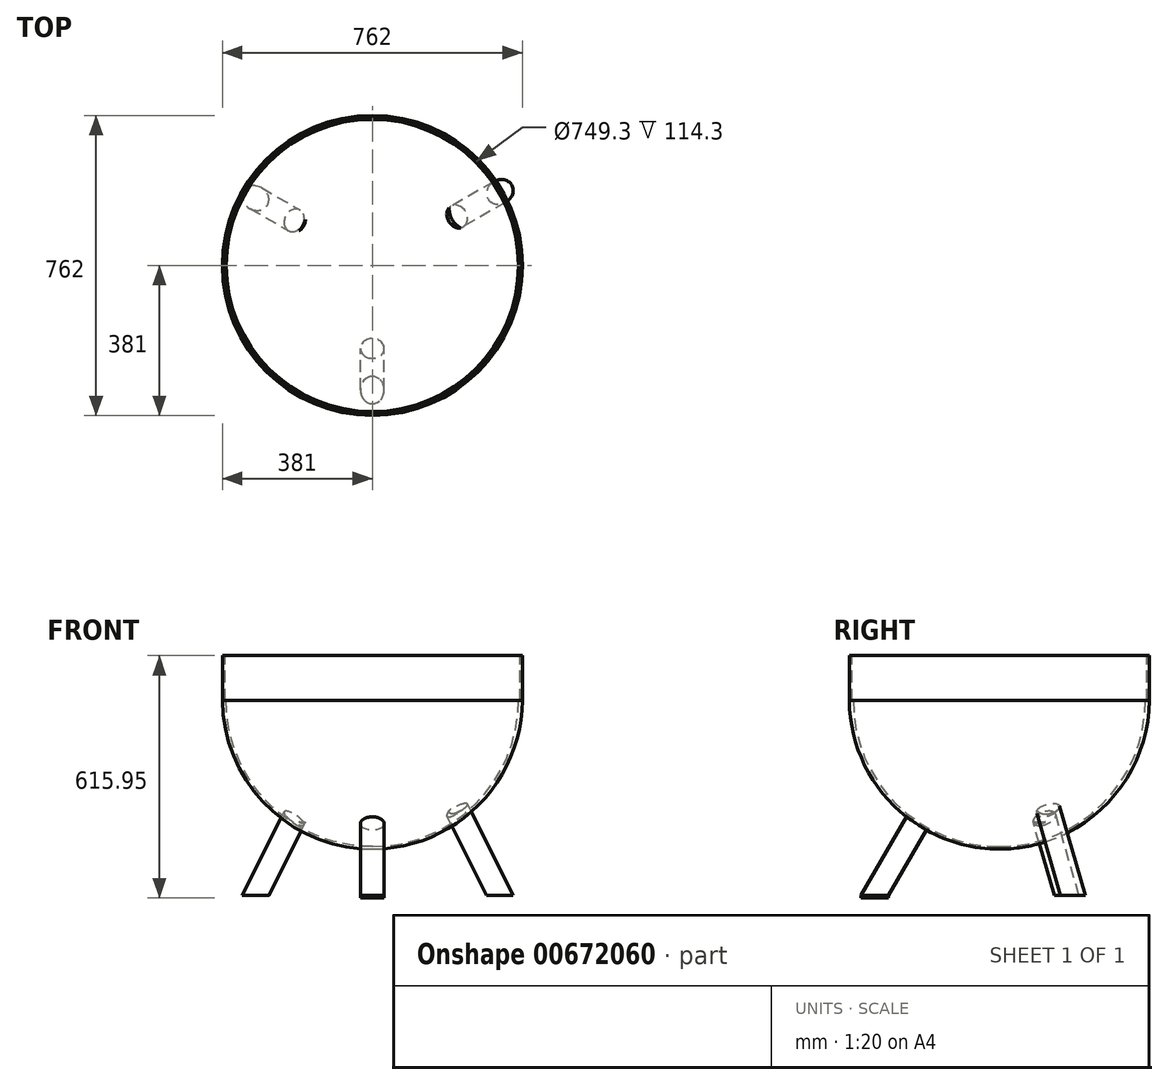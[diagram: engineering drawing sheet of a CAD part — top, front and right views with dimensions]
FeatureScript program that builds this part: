
annotation { "Feature Type Name" : "Feature", "Feature Type Description" : "" }
export const myFeature = defineFeature(function(context is Context, id is Id, definition is map)
    precondition{}
    {
        {
            var Q0;
            Q0=qCreatedBy(makeId("Top.planeOp"),FACE);
            var sketch = newSketch(context, id + "F0", { "sketchPlane" : qUnion([Q0])});
            skCircle(sketch, "E0.cCircle", {"center": v(0, 0) * mm, "radius": 527.93 * mm, "construction": true});
            skLineSegment(sketch, "E0.0", {"start": v(304.8, 527.93) * mm, "end": v(609.6, 0) * mm});
            skLineSegment(sketch, "E0.1", {"start": v(609.6, 0) * mm, "end": v(457.2, -263.96) * mm});
            skLineSegment(sketch, "E0.2", {"start": v(304.8, -527.93) * mm, "end": v(-304.8, -527.93) * mm});
            skLineSegment(sketch, "E0.3", {"start": v(-304.8, -527.93) * mm, "end": v(-457.2, -263.96) * mm});
            skLineSegment(sketch, "E0.4", {"start": v(-609.6, 0) * mm, "end": v(-450.85, 274.96) * mm});
            skLineSegment(sketch, "E0.5", {"start": v(-304.8, 527.93) * mm, "end": v(0, 527.93) * mm});
            skPoint(sketch, "E0.0.midPoint", {"position": v(457.2, 263.96) * mm});
            skCircle(sketch, "E1", {"center": v(0, 0) * mm, "radius": 381 * mm});
            skLineSegment(sketch, "E2", {"start": v(-463.55, 252.97) * mm, "end": v(-336.12, 179.4) * mm});
            skLineSegment(sketch, "E3", {"start": v(-450.85, 274.96) * mm, "end": v(-323.42, 201.4) * mm});
            skLineSegment(sketch, "E4", {"start": v(-304.8, 527.93) * mm, "end": v(-304.8, 527.93) * mm});
            skLineSegment(sketch, "E5", {"start": v(-463.55, 252.97) * mm, "end": v(-304.8, 527.93) * mm});
            skLineSegment(sketch, "E6", {"start": v(-450.85, 274.96) * mm, "end": v(-401.2, 360.95) * mm});
            skLineSegment(sketch, "E7", {"start": v(-609.6, 0) * mm, "end": v(-609.6, 0) * mm});
            skLineSegment(sketch, "E8.1.0", {"start": v(-450.85, -274.96) * mm, "end": v(-323.42, -201.4) * mm});
            skLineSegment(sketch, "E8.1.1", {"start": v(-463.55, -252.97) * mm, "end": v(-336.12, -179.4) * mm});
            skLineSegment(sketch, "E8.2.0", {"start": v(12.7, -527.93) * mm, "end": v(12.7, -380.79) * mm});
            skLineSegment(sketch, "E8.2.1", {"start": v(-12.7, -527.93) * mm, "end": v(-12.7, -380.79) * mm});
            skLineSegment(sketch, "E8.3.0", {"start": v(463.55, -252.97) * mm, "end": v(336.12, -179.4) * mm});
            skLineSegment(sketch, "E8.3.1", {"start": v(450.85, -274.96) * mm, "end": v(323.42, -201.4) * mm});
            skLineSegment(sketch, "E8.4.0", {"start": v(450.85, 274.96) * mm, "end": v(323.42, 201.4) * mm});
            skLineSegment(sketch, "E8.4.1", {"start": v(463.55, 252.97) * mm, "end": v(336.12, 179.4) * mm});
            skLineSegment(sketch, "E8.5.0", {"start": v(-12.7, 527.93) * mm, "end": v(-12.7, 380.79) * mm});
            skLineSegment(sketch, "E8.5.1", {"start": v(12.7, 527.93) * mm, "end": v(12.7, 380.79) * mm});
            skLineSegment(sketch, "E9", {"start": v(-1099.5, 381) * mm, "end": v(1284.02, 381) * mm, "construction": true});
            skLineSegment(sketch, "E10", {"start": v(-1101.82, -381) * mm, "end": v(1466.6, -381) * mm, "construction": true});
            skLineSegment(sketch, "E11", {"start": v(127, -73.32) * mm, "end": v(-127, -73.32) * mm});
            skCircle(sketch, "E12", {"center": v(0, 0) * mm, "radius": 146.65 * mm, "construction": true});
            skLineSegment(sketch, "E13", {"start": v(0, 0) * mm, "end": v(329.96, -190.5) * mm, "construction": true});
            skLineSegment(sketch, "E14", {"start": v(0, 0) * mm, "end": v(-329.96, -190.5) * mm, "construction": true});
            skLineSegment(sketch, "E15", {"start": v(0, 0) * mm, "end": v(0, 381) * mm, "construction": true});
            skLineSegment(sketch, "E16", {"start": v(329.96, -190.5) * mm, "end": v(1171.58, -676.41) * mm, "construction": true});
            skLineSegment(sketch, "E17", {"start": v(457.2, -263.96) * mm, "end": v(304.8, -527.93) * mm});
            skLineSegment(sketch, "E18", {"start": v(329.96, -190.5) * mm, "end": v(457.2, -263.96) * mm});
            skLineSegment(sketch, "E19", {"start": v(0, 381) * mm, "end": v(0, 1090.4) * mm, "construction": true});
            skLineSegment(sketch, "E20", {"start": v(0, 527.93) * mm, "end": v(304.8, 527.93) * mm});
            skLineSegment(sketch, "E21", {"start": v(0, 527.93) * mm, "end": v(0, 381) * mm});
            skLineSegment(sketch, "E22", {"start": v(-329.96, -190.5) * mm, "end": v(-1262.9, -729.14) * mm, "construction": true});
            skLineSegment(sketch, "E23", {"start": v(-457.2, -263.96) * mm, "end": v(-609.6, 0) * mm});
            skLineSegment(sketch, "E24", {"start": v(-329.96, -190.5) * mm, "end": v(-457.2, -263.96) * mm});
            skCircle(sketch, "E25", {"center": v(0, 0) * mm, "radius": 374.65 * mm});
            skSolve(sketch);
        }
        {
            var Q0;
            {var subQ0=sQuery(id+"F0.wireOp",EDGE,"E1");var subQ8=makeQuery(id+"F0.imprint","INTERSECT",VERTEX,{"derivedFrom":[subQ0,sQuery(id+"F0.wireOp",EDGE,"E8.4.0")]});Q0=makeQuery(id+"F0.imprint","IMPRINT",FACE,{"disambiguationData":[TD([[makeQuery(id+"F0.imprint","IMPRINT",EDGE,{"disambiguationData":[TD([[subQ8,1.0]])],"derivedFrom":subQ0}),1.0]])]});}
            extrude(context, id + "F1", {"entities" : qUnion([Q0]), "oppositeDirection" : true, "depth" : 152.4 * mm, "offsetDistance" : 25.4 * mm, "hasSecondDirection" : true, "secondDirectionOppositeDirection" : true, "secondDirectionDepth" : 38.1 * mm});
        }
        {
            var Q0;
            Q0=qCreatedBy(makeId("Front.planeOp"),FACE);
            var sketch = newSketch(context, id + "F2", { "sketchPlane" : qUnion([Q0])});
            skLineSegment(sketch, "E26", {"start": v(0, 608.83) * mm, "end": v(0, -1105.26) * mm, "construction": true});
            skLineSegment(sketch, "E27", {"start": v(-381, 462.6) * mm, "end": v(-381, -843.09) * mm});
            skLineSegment(sketch, "E28.MirrorCS", {"start": v(381, 462.6) * mm, "end": v(381, -843.09) * mm});
            skLineSegment(sketch, "E29", {"start": v(-1108.33, -152.4) * mm, "end": v(1492.5, -152.4) * mm, "construction": true});
            skArc(sketch, "E30", {"start": v(-381, -152.4) * mm, "mid": v(-268.19, -419.57) * mm, "end": v(0, -529.94) * mm});
            skArc(sketch, "E31", {"start": v(0, -529.94) * mm, "mid": v(268.19, -419.57) * mm, "end": v(381, -152.4) * mm});
            skLineSegment(sketch, "E32", {"start": v(-495.68, -152.4) * mm, "end": v(0, -152.4) * mm});
            skLineSegment(sketch, "E33", {"start": v(0, 45.3) * mm, "end": v(0, -541.67) * mm});
            skLineSegment(sketch, "E34", {"start": v(0, -152.4) * mm, "end": v(518.85, -152.4) * mm});
            skCircle(sketch, "E35", {"center": v(0, -152.4) * mm, "radius": 371.19 * mm});
            skSolve(sketch);
        }
        {
            var Q0;
            Q0=sQuery(id+"F0.wireOp",EDGE,"E13");
            var Q1;
            Q1=sQuery(id+"F2.wireOp",EDGE,"E26");
            cPlane(context, id + "F3", {"entities" : qUnion([Q0, Q1]), "cplaneType" : CPlaneType.LINE_ANGLE, "offset" : 25.4 * mm, "angle" : 0 * degree, "width" : 152.4 * mm, "height" : 152.4 * mm});
        }
        {
            var Q0;
            Q0=sQuery(id+"F0.wireOp",EDGE,"E15");
            var Q1;
            Q1=sQuery(id+"F2.wireOp",EDGE,"E26");
            cPlane(context, id + "F4", {"entities" : qUnion([Q0, Q1]), "cplaneType" : CPlaneType.LINE_ANGLE, "offset" : 25.4 * mm, "angle" : 0 * degree, "width" : 152.4 * mm, "height" : 152.4 * mm});
        }
        {
            var Q0;
            Q0=sQuery(id+"F0.wireOp",EDGE,"E22");
            var Q1;
            Q1=sQuery(id+"F2.wireOp",EDGE,"E26");
            cPlane(context, id + "F5", {"entities" : qUnion([Q0, Q1]), "cplaneType" : CPlaneType.LINE_ANGLE, "offset" : 25.4 * mm, "angle" : 0 * degree, "width" : 152.4 * mm, "height" : 152.4 * mm});
        }
        {
            var Q0;
            Q0=qCreatedBy(id+"F5.planeOp",FACE);
            var sketch = newSketch(context, id + "F6", { "sketchPlane" : qUnion([Q0])});
            skLineSegment(sketch, "E36", {"start": v(-1017.96, -647.7) * mm, "end": v(-373.95, -647.7) * mm});
            skLineSegment(sketch, "E37", {"start": v(-2207.22, 0) * mm, "end": v(364.68, 0) * mm, "construction": true});
            skLineSegment(sketch, "E38", {"start": v(0, 853.8) * mm, "end": v(0, -860.28) * mm, "construction": true});
            skLineSegment(sketch, "E39", {"start": v(-381, 707.57) * mm, "end": v(-381, -944.4) * mm});
            skLineSegment(sketch, "E40", {"start": v(-2225.52, -152.4) * mm, "end": v(0, -152.4) * mm, "construction": true});
            skArc(sketch, "E41", {"start": v(-381, -152.4) * mm, "mid": v(-268.19, -419.57) * mm, "end": v(0, -529.94) * mm});
            skArc(sketch, "E42", {"start": v(0, -529.94) * mm, "mid": v(268.19, -419.57) * mm, "end": v(381, -152.4) * mm});
            skLineSegment(sketch, "E43", {"start": v(0, -152.4) * mm, "end": v(375.32, -152.4) * mm, "construction": true});
            skLineSegment(sketch, "E44", {"start": v(-1487.46, 0) * mm, "end": v(0, 0) * mm, "construction": true});
            skLineSegment(sketch, "E45", {"start": v(-470.85, 0) * mm, "end": v(0, 0) * mm, "construction": true});
            skLineSegment(sketch, "E46", {"start": v(277.13, -647.7) * mm, "end": v(310.58, -647.7) * mm});
            skLineSegment(sketch, "E47", {"start": v(0, 0) * mm, "end": v(-373.95, -647.7) * mm});
            skLineSegment(sketch, "E48", {"start": v(32.55, -3.98) * mm, "end": v(-339.1, -647.7) * mm});
            skLineSegment(sketch, "E49", {"start": v(-34.84, 0) * mm, "end": v(-408.8, -647.7) * mm});
            skLineSegment(sketch, "E50", {"start": v(-381, -647.7) * mm, "end": v(1871, -647.7) * mm});
            skLineSegment(sketch, "E51.MirrorCS", {"start": v(34.84, 0) * mm, "end": v(408.8, -647.7) * mm});
            skLineSegment(sketch, "E52.MirrorCS", {"start": v(-32.55, -3.98) * mm, "end": v(339.1, -647.7) * mm});
            skLineSegment(sketch, "E53.MirrorCS", {"start": v(0, 0) * mm, "end": v(373.95, -647.7) * mm});
            skSolve(sketch);
        }
        {
            var Q0;
            {var subQ0=sQuery(id+"F6.wireOp",EDGE,"E51.MirrorCS");var subQ1=sQuery(id+"F6.wireOp",EDGE,"E42");var subQ2=makeQuery(id+"F6.imprint","INTERSECT",VERTEX,{"derivedFrom":[subQ1,subQ0]});Q0=makeQuery(id+"F6.imprint","IMPRINT",FACE,{"disambiguationData":[TD([[makeQuery(id+"F6.imprint","IMPRINT",EDGE,{"disambiguationData":[TD([[subQ2,1.0]])],"derivedFrom":subQ1}),-1.0]])]});}
            var Q1;
            Q1=sQuery(id+"F6.wireOp",EDGE,"E53.MirrorCS");
            revolve(context, id + "F7", {"entities" : qUnion([Q0]), "axis" : qUnion([Q1]), "revolveType" : RevolveType.FULL});
        }
        {
            var Q0;
            {var subQ0=sQuery(id+"F2.wireOp",EDGE,"E31");Q0=makeQuery(id+"F2.imprint","IMPRINT",FACE,{"disambiguationData":[TD([[makeQuery(id+"F2.imprint","IMPRINT",EDGE,{"derivedFrom":subQ0}),1.0]])]});}
            var Q1;
            Q1=sQuery(id+"F2.wireOp",EDGE,"E33");
            revolve(context, id + "F8", {"entities" : qUnion([Q0]), "axis" : qUnion([Q1]), "revolveType" : RevolveType.FULL});
        }
        {
            var Q0;
            {var subQ0=sQuery(id+"F2.wireOp",EDGE,"E34");var subQ3=sQuery(id+"F2.wireOp",EDGE,"E35");var subQ5=makeQuery(id+"F2.imprint","INTERSECT",VERTEX,{"derivedFrom":[subQ0,subQ3]});Q0=makeQuery(id+"F2.imprint","IMPRINT",FACE,{"disambiguationData":[TD([[makeQuery(id+"F2.imprint","IMPRINT",EDGE,{"disambiguationData":[TD([[subQ5,1.0]])],"derivedFrom":subQ3}),1.0]])]});}
            var Q1;
            Q1=sQuery(id+"F2.wireOp",EDGE,"E33");
            revolve(context, id + "F9", {"operationType" : NewBodyOperationType.REMOVE, "entities" : qUnion([Q0]), "axis" : qUnion([Q1]), "revolveType" : RevolveType.FULL, "oppositeDirection" : true});
        }
        {
            var Q0;
            {var subQ0=sQuery(id+"F0.wireOp",EDGE,"E8.1.0");Q0=makeQuery(id+"F0.imprint","IMPRINT",FACE,{"disambiguationData":[TD([[makeQuery(id+"F0.imprint","IMPRINT",EDGE,{"derivedFrom":subQ0}),-1.0]])]});}
            cPlane(context, id + "F10", {"entities" : qUnion([Q0]), "cplaneType" : CPlaneType.OFFSET, "offset" : 647.7 * mm, "oppositeDirection" : true, "width" : 152.4 * mm, "height" : 152.4 * mm});
        }
        {
            var Q0;
            Q0=qCreatedBy(id+"F10.planeOp",FACE);
            var sketch = newSketch(context, id + "F11", { "sketchPlane" : qUnion([Q0])});
            skLineSegment(sketch, "E54.bottom", {"start": v(-408.5, 256.07) * mm, "end": v(423.7, 256.07) * mm});
            skLineSegment(sketch, "E54.top", {"start": v(-408.5, -410.84) * mm, "end": v(423.7, -410.84) * mm});
            skLineSegment(sketch, "E54.left", {"start": v(-408.5, 256.07) * mm, "end": v(-408.5, -410.84) * mm});
            skLineSegment(sketch, "E54.right", {"start": v(423.7, 256.07) * mm, "end": v(423.7, -410.84) * mm});
            skSolve(sketch);
        }
        {
            var Q0;
            Q0=qSketchRegion(id+"F11",true);
            extrude(context, id + "F12", {"entities" : qUnion([Q0]), "operationType" : NewBodyOperationType.REMOVE, "oppositeDirection" : true, "depth" : 50.8 * mm, "offsetDistance" : 25.4 * mm});
        }
        {
            var Q0;
            Q0=qCreatedBy(id+"F3.planeOp",FACE);
            var sketch = newSketch(context, id + "F13", { "sketchPlane" : qUnion([Q0])});
            skLineSegment(sketch, "E55", {"start": v(-1049.37, -647.7) * mm, "end": v(-342.54, -647.7) * mm});
            skLineSegment(sketch, "E56", {"start": v(-2238.63, 0) * mm, "end": v(333.27, 0) * mm, "construction": true});
            skLineSegment(sketch, "E57", {"start": v(0, 853.8) * mm, "end": v(0, -860.28) * mm, "construction": true});
            skLineSegment(sketch, "E58", {"start": v(-381, 707.57) * mm, "end": v(-381, -944.4) * mm});
            skLineSegment(sketch, "E59", {"start": v(-2225.52, -152.4) * mm, "end": v(0, -152.4) * mm, "construction": true});
            skArc(sketch, "E60", {"start": v(-381, -152.4) * mm, "mid": v(-268.19, -419.57) * mm, "end": v(0, -529.94) * mm});
            skArc(sketch, "E61", {"start": v(0, -529.94) * mm, "mid": v(268.19, -419.57) * mm, "end": v(381, -152.4) * mm});
            skLineSegment(sketch, "E62", {"start": v(0, -152.4) * mm, "end": v(375.32, -152.4) * mm, "construction": true});
            skLineSegment(sketch, "E63", {"start": v(-1518.87, 0) * mm, "end": v(0, 0) * mm, "construction": true});
            skLineSegment(sketch, "E64", {"start": v(-502.26, 0) * mm, "end": v(0, 0) * mm, "construction": true});
            skLineSegment(sketch, "E65", {"start": v(245.72, -647.7) * mm, "end": v(310.58, -647.7) * mm});
            skLineSegment(sketch, "E66", {"start": v(31.4, 0) * mm, "end": v(-342.54, -647.7) * mm});
            skLineSegment(sketch, "E67", {"start": v(63.96, -3.98) * mm, "end": v(-307.7, -647.7) * mm});
            skLineSegment(sketch, "E68", {"start": v(-3.43, 0) * mm, "end": v(-377.38, -647.7) * mm});
            skLineSegment(sketch, "E69", {"start": v(-381, -647.7) * mm, "end": v(1839.6, -647.7) * mm});
            skLineSegment(sketch, "E70.MirrorCS", {"start": v(3.43, 0) * mm, "end": v(377.38, -647.7) * mm});
            skLineSegment(sketch, "E71.MirrorCS", {"start": v(-63.96, -3.98) * mm, "end": v(307.7, -647.7) * mm});
            skLineSegment(sketch, "E72.MirrorCS", {"start": v(-31.4, 0) * mm, "end": v(342.54, -647.7) * mm});
            skSolve(sketch);
        }
        {
            var Q0;
            {var subQ0=sQuery(id+"F13.wireOp",EDGE,"E70.MirrorCS");var subQ1=sQuery(id+"F13.wireOp",EDGE,"E61");var subQ2=makeQuery(id+"F13.imprint","INTERSECT",VERTEX,{"derivedFrom":[subQ1,subQ0]});Q0=makeQuery(id+"F13.imprint","IMPRINT",FACE,{"disambiguationData":[TD([[makeQuery(id+"F13.imprint","IMPRINT",EDGE,{"disambiguationData":[TD([[subQ2,1.0]])],"derivedFrom":subQ1}),-1.0]])]});}
            var Q1;
            Q1=sQuery(id+"F13.wireOp",EDGE,"E72.MirrorCS");
            revolve(context, id + "F14", {"operationType" : NewBodyOperationType.ADD, "entities" : qUnion([Q0]), "axis" : qUnion([Q1]), "revolveType" : RevolveType.FULL});
        }
        {
            var Q0;
            Q0=qCreatedBy(id+"F4.planeOp",FACE);
            var sketch = newSketch(context, id + "F15", { "sketchPlane" : qUnion([Q0])});
            skLineSegment(sketch, "E73", {"start": v(-1075.54, -647.7) * mm, "end": v(-316.37, -647.7) * mm});
            skLineSegment(sketch, "E74", {"start": v(-2264.8, 0) * mm, "end": v(307.1, 0) * mm, "construction": true});
            skLineSegment(sketch, "E75", {"start": v(0, 1137.28) * mm, "end": v(0, -576.81) * mm, "construction": true});
            skLineSegment(sketch, "E76", {"start": v(-381, 707.57) * mm, "end": v(-381, -944.4) * mm});
            skLineSegment(sketch, "E77", {"start": v(-2225.52, -152.4) * mm, "end": v(0, -152.4) * mm, "construction": true});
            skArc(sketch, "E78", {"start": v(-381, -152.4) * mm, "mid": v(-268.19, -419.57) * mm, "end": v(0, -529.94) * mm});
            skArc(sketch, "E79", {"start": v(0, -529.94) * mm, "mid": v(268.19, -419.57) * mm, "end": v(381, -152.4) * mm});
            skLineSegment(sketch, "E80", {"start": v(0, -152.4) * mm, "end": v(375.32, -152.4) * mm, "construction": true});
            skLineSegment(sketch, "E81", {"start": v(-1545.05, 0) * mm, "end": v(0, 0) * mm, "construction": true});
            skLineSegment(sketch, "E82", {"start": v(-528.43, 0) * mm, "end": v(0, 0) * mm, "construction": true});
            skLineSegment(sketch, "E83", {"start": v(219.55, -647.7) * mm, "end": v(310.58, -647.7) * mm});
            skLineSegment(sketch, "E84", {"start": v(57.58, 0) * mm, "end": v(-316.37, -647.7) * mm});
            skLineSegment(sketch, "E85", {"start": v(90.13, -3.98) * mm, "end": v(-281.52, -647.7) * mm});
            skLineSegment(sketch, "E86", {"start": v(22.74, 0) * mm, "end": v(-351.2, -647.7) * mm});
            skLineSegment(sketch, "E87", {"start": v(-381, -647.7) * mm, "end": v(1813.42, -647.7) * mm});
            skLineSegment(sketch, "E88.MirrorCS", {"start": v(-22.74, 0) * mm, "end": v(351.2, -647.7) * mm});
            skLineSegment(sketch, "E89.MirrorCS", {"start": v(-90.13, -3.98) * mm, "end": v(281.52, -647.7) * mm});
            skLineSegment(sketch, "E90.MirrorCS", {"start": v(-57.58, 0) * mm, "end": v(316.37, -647.7) * mm});
            skSolve(sketch);
        }
        {
            var Q0;
            {var subQ0=sQuery(id+"F15.wireOp",EDGE,"E88.MirrorCS");var subQ1=sQuery(id+"F15.wireOp",EDGE,"E79");var subQ2=makeQuery(id+"F15.imprint","INTERSECT",VERTEX,{"derivedFrom":[subQ1,subQ0]});Q0=makeQuery(id+"F15.imprint","IMPRINT",FACE,{"disambiguationData":[TD([[makeQuery(id+"F15.imprint","IMPRINT",EDGE,{"disambiguationData":[TD([[subQ2,1.0]])],"derivedFrom":subQ1}),-1.0]])]});}
            var Q1;
            Q1=sQuery(id+"F15.wireOp",EDGE,"E90.MirrorCS");
            revolve(context, id + "F16", {"operationType" : NewBodyOperationType.ADD, "entities" : qUnion([Q0]), "axis" : qUnion([Q1]), "revolveType" : RevolveType.FULL});
        }
        {
            var Q0;
            Q0=qSketchRegion(id+"F11",true);
            extrude(context, id + "F17", {"entities" : qUnion([Q0]), "operationType" : NewBodyOperationType.REMOVE, "oppositeDirection" : true, "depth" : 50.8 * mm, "offsetDistance" : 25.4 * mm});
        }
        {
            var Q0;
            Q0=makeQuery(id+"F17.boolean.opBoolean","COPY",FACE,{"disambiguationData":[TD([makeQuery(id+"F16.opRevolve","SWEPT_FACE",FACE,{"disambiguationData":[OSD([sQuery(id+"F15.wireOp",EDGE,"E88.MirrorCS")])]})])],"derivedFrom":makeQuery(id+"F17.opExtrude","CAP_FACE",FACE,{"disambiguationData":[OSD([sQuery(id+"F11.wireOp",EDGE,"E54.bottom"),sQuery(id+"F11.wireOp",EDGE,"E54.top"),sQuery(id+"F11.wireOp",EDGE,"E54.left"),sQuery(id+"F11.wireOp",EDGE,"E54.right")])],"isStart":true})});
            extrude(context, id + "F18", {"entities" : qUnion([Q0]), "depth" : 6.35 * mm, "offsetDistance" : 25.4 * mm});
        }
    });
